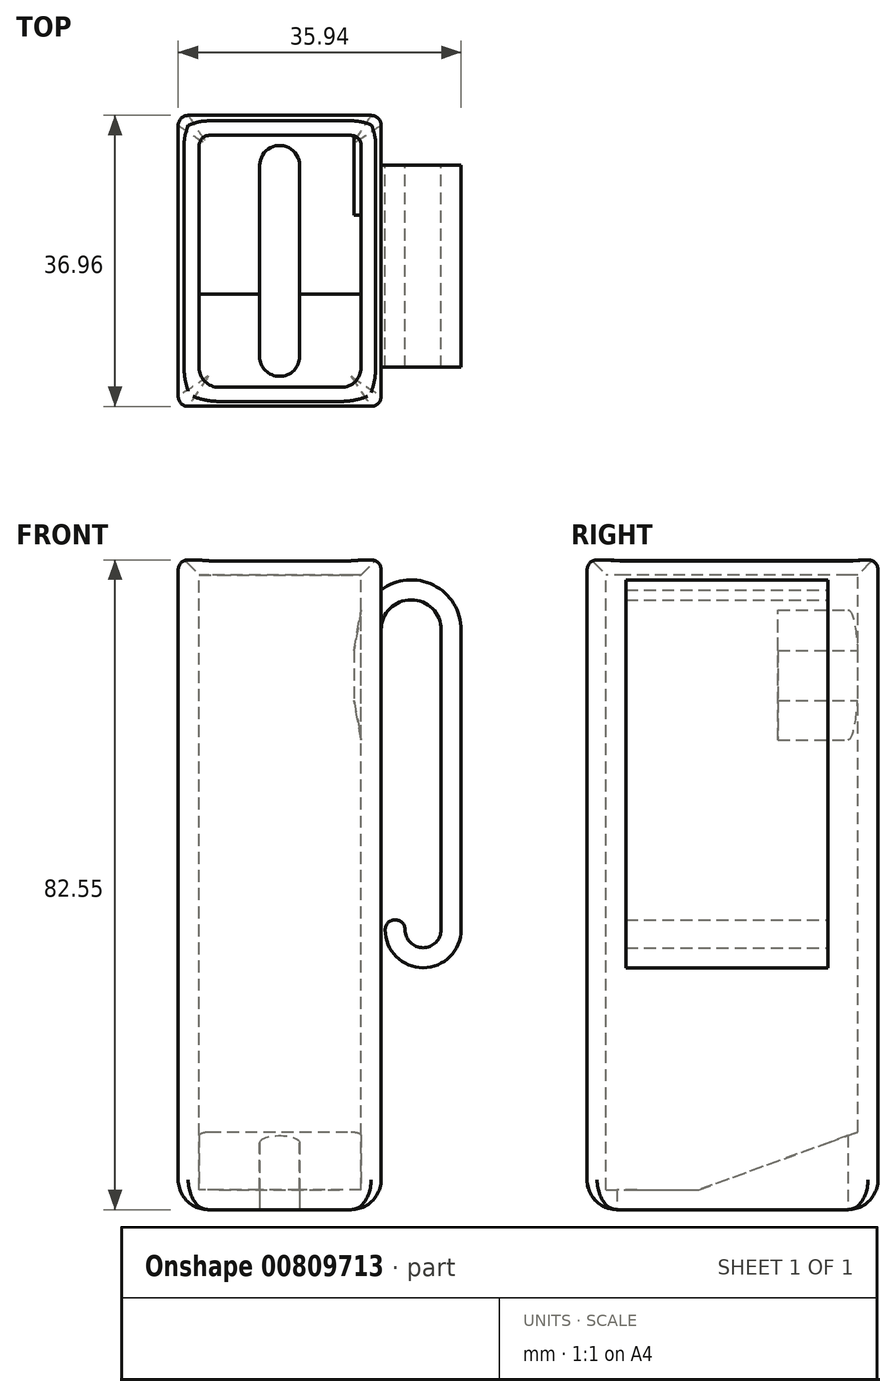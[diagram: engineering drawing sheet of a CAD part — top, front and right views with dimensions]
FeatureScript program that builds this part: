
annotation { "Feature Type Name" : "Feature", "Feature Type Description" : "" }
export const myFeature = defineFeature(function(context is Context, id is Id, definition is map)
    precondition{}
    {
        {
            var Q0;
            Q0=qCreatedBy(makeId("Front.planeOp"),FACE);
            var sketch = newSketch(context, id + "F0", { "sketchPlane" : qUnion([Q0])});
            skLineSegment(sketch, "E0.bottom", {"start": v(-10.35, 0) * mm, "end": v(10.35, 0) * mm});
            skLineSegment(sketch, "E0.top", {"start": v(-10.35, 82.55) * mm, "end": v(10.35, 82.55) * mm});
            skLineSegment(sketch, "E0.left", {"start": v(-10.35, 0) * mm, "end": v(-10.35, 82.55) * mm});
            skLineSegment(sketch, "E0.right", {"start": v(10.35, 0) * mm, "end": v(10.35, 82.55) * mm});
            skSolve(sketch);
        }
        {
            var Q0;
            Q0 = qSketchRegion(id + "F0", true);
            extrude(context, id + "F1", {"entities" : qUnion([Q0]), "depth" : 31.88 * mm, "offsetDistance" : 25.4 * mm});
        }
        {
            var Q0;
            Q0=makeQuery(id+"F1.opExtrude","SWEPT_FACE",FACE,{"disambiguationData":[OSD([sQuery(id+"F0.wireOp",EDGE,"E0.right")])]});
            extrude(context, id + "F2", {"entities" : qUnion([Q0]), "operationType" : NewBodyOperationType.ADD, "depth" : 5.08 * mm, "offsetDistance" : 25.4 * mm});
        }
        {
            var Q0;
            {var subQ0=sQuery(id+"F0.wireOp",EDGE,"E0.right");Q0=makeQuery(id+"F2.boolean.opBoolean","MERGE",FACE,{"derivedFrom":[makeQuery(id+"F1.opExtrude","CAP_FACE",FACE,{"disambiguationData":[OSD([sQuery(id+"F0.wireOp",EDGE,"E0.bottom"),sQuery(id+"F0.wireOp",EDGE,"E0.top"),sQuery(id+"F0.wireOp",EDGE,"E0.left"),subQ0])],"isStart":false}),makeQuery(id+"F2.opExtrude","SWEPT_FACE",FACE,{"disambiguationData":[OSD([subQ0]),TDD([makeQuery(id+"F1.opExtrude","CAP_EDGE",EDGE,{"disambiguationData":[OSD([subQ0])],"isStart":false})])]})]});}
            extrude(context, id + "F3", {"entities" : qUnion([Q0]), "operationType" : NewBodyOperationType.ADD, "depth" : 5.08 * mm, "offsetDistance" : 25.4 * mm});
        }
        {
            var Q0;
            {var subQ0=sQuery(id+"F0.wireOp",EDGE,"E0.right");var subQ1=sQuery(id+"F0.wireOp",EDGE,"E0.bottom");Q0=makeQuery(id+"F2.boolean.opBoolean","MERGE",EDGE,{"derivedFrom":[makeQuery(id+"F1.opExtrude","CAP_EDGE",EDGE,{"disambiguationData":[OSD([subQ1])],"isStart":true}),makeQuery(id+"F2.opExtrude","SWEPT_EDGE",EDGE,{"disambiguationData":[OSD([subQ1,subQ0]),TDD([makeQuery(id+"F1.opExtrude","CAP_VERTEX",VERTEX,{"disambiguationData":[OSD([subQ1,subQ0])],"isStart":true})])]})]});}
            cPlane(context, id + "F4", {"entities" : qUnion([Q0]), "cplaneType" : CPlaneType.LINE_ANGLE, "offset" : 25.4 * mm, "angle" : 70 * degree, "oppositeDirection" : true, "width" : 152.4 * mm, "height" : 152.4 * mm});
        }
        {
            var Q0;
            Q0=qCreatedBy(id+"F4.planeOp",FACE);
            cPlane(context, id + "F5", {"entities" : qUnion([Q0]), "cplaneType" : CPlaneType.OFFSET, "offset" : 10.16 * mm, "oppositeDirection" : true, "width" : 152.4 * mm, "height" : 152.4 * mm});
        }
        {
            var Q0;
            {var subQ0=sQuery(id+"F0.wireOp",EDGE,"E0.right");var subQ1=sQuery(id+"F0.wireOp",EDGE,"E0.top");Q0=makeQuery(id+"F3.boolean.opBoolean","MERGE",FACE,{"derivedFrom":[makeQuery(id+"F2.boolean.opBoolean","MERGE",FACE,{"derivedFrom":[makeQuery(id+"F1.opExtrude","SWEPT_FACE",FACE,{"disambiguationData":[OSD([subQ1])]}),makeQuery(id+"F2.opExtrude","SWEPT_FACE",FACE,{"disambiguationData":[OSD([subQ1,subQ0])]})]}),makeQuery(id+"F3.opExtrude","SWEPT_FACE",FACE,{"disambiguationData":[OSD([subQ1,subQ0])]})]});}
            var sketch = newSketch(context, id + "F6", { "sketchPlane" : qUnion([Q0])});
            skLineSegment(sketch, "E1.bottom", {"start": v(-7.68, -2.54) * mm, "end": v(12.9, -2.54) * mm});
            skLineSegment(sketch, "E1.top", {"start": v(-7.68, -34.54) * mm, "end": v(12.9, -34.54) * mm});
            skLineSegment(sketch, "E1.left", {"start": v(-7.68, -2.54) * mm, "end": v(-7.68, -34.54) * mm});
            skLineSegment(sketch, "E1.right", {"start": v(12.9, -2.54) * mm, "end": v(12.9, -34.54) * mm});
            skSolve(sketch);
        }
        {
            var Q0;
            Q0 = qSketchRegion(id + "F6", true);
            var Q1;
            Q1=qCreatedBy(id+"F5.planeOp",FACE);
            extrude(context, id + "F7", {"entities" : qUnion([Q0]), "operationType" : NewBodyOperationType.REMOVE, "endBound" : BoundingType.UP_TO_SURFACE, "oppositeDirection" : true, "depth" : 25.4 * mm, "endBoundEntityFace" : qUnion([Q1]), "offsetDistance" : 25.4 * mm});
        }
        {
            var Q0;
            Q0=qCreatedBy(makeId("Right.planeOp"),FACE);
            var sketch = newSketch(context, id + "F8", { "sketchPlane" : qUnion([Q0])});
            skLineSegment(sketch, "E2.bottom", {"start": v(-34.93, 0) * mm, "end": v(-22.23, 0) * mm});
            skLineSegment(sketch, "E2.top", {"start": v(-34.93, 2.54) * mm, "end": v(-22.23, 2.54) * mm});
            skLineSegment(sketch, "E2.left", {"start": v(-34.93, 0) * mm, "end": v(-34.93, 2.54) * mm});
            skLineSegment(sketch, "E2.right", {"start": v(-22.23, 0) * mm, "end": v(-22.23, 2.54) * mm});
            skSolve(sketch);
        }
        {
            var Q0;
            Q0 = qSketchRegion(id + "F8", true);
            var Q1;
            Q1=makeQuery(id+"F7.boolean.opBoolean","COPY",FACE,{"derivedFrom":makeQuery(id+"F7.opExtrude","SWEPT_FACE",FACE,{"disambiguationData":[OSD([sQuery(id+"F6.wireOp",EDGE,"E1.left")])]})});
            var Q2;
            Q2=makeQuery(id+"F7.boolean.opBoolean","COPY",FACE,{"derivedFrom":makeQuery(id+"F7.opExtrude","SWEPT_FACE",FACE,{"disambiguationData":[OSD([sQuery(id+"F6.wireOp",EDGE,"E1.right")])]})});
            extrude(context, id + "F9", {"entities" : qUnion([Q0]), "operationType" : NewBodyOperationType.ADD, "endBound" : BoundingType.UP_TO_SURFACE, "oppositeDirection" : true, "depth" : 25.4 * mm, "endBoundEntityFace" : qUnion([Q1]), "offsetDistance" : 25.4 * mm, "hasSecondDirection" : true, "secondDirectionBound" : SecondDirectionBoundingType.UP_TO_SURFACE, "secondDirectionOppositeDirection" : false, "secondDirectionDepth" : 25.4 * mm, "secondDirectionBoundEntityFace" : qUnion([Q2])});
        }
        {
            var Q0;
            {var subQ0=sQuery(id+"F0.wireOp",EDGE,"E0.right");var subQ1=sQuery(id+"F0.wireOp",EDGE,"E0.bottom");Q0=makeQuery(id+"F9.boolean.opBoolean","MERGE",FACE,{"derivedFrom":[makeQuery(id+"F3.boolean.opBoolean","MERGE",FACE,{"derivedFrom":[makeQuery(id+"F2.boolean.opBoolean","MERGE",FACE,{"derivedFrom":[makeQuery(id+"F1.opExtrude","SWEPT_FACE",FACE,{"disambiguationData":[OSD([subQ1])]}),makeQuery(id+"F2.opExtrude","SWEPT_FACE",FACE,{"disambiguationData":[OSD([subQ1,subQ0])]})]}),makeQuery(id+"F3.opExtrude","SWEPT_FACE",FACE,{"disambiguationData":[OSD([subQ1,subQ0])]})]}),makeQuery(id+"F9.opExtrude","SWEPT_FACE",FACE,{"disambiguationData":[OSD([sQuery(id+"F8.wireOp",EDGE,"E2.bottom")])]})]});}
            var sketch = newSketch(context, id + "F10", { "sketchPlane" : qUnion([Q0])});
            skPoint(sketch, "E3.startSnap0", {"position": v(2.54, 36.96) * mm});
            skLineSegment(sketch, "E4.left", {"start": v(0, 30.6) * mm, "end": v(0, 6.35) * mm});
            skLineSegment(sketch, "E4.right", {"start": v(5.08, 30.6) * mm, "end": v(5.08, 6.35) * mm});
            skArc(sketch, "E5", {"start": v(0, 30.6) * mm, "mid": v(2.54, 33.15) * mm, "end": v(5.08, 30.6) * mm});
            skArc(sketch, "E6", {"start": v(0, 6.35) * mm, "mid": v(2.54, 3.8) * mm, "end": v(5.08, 6.35) * mm});
            skSolve(sketch);
        }
        {
            var Q0;
            Q0 = qSketchRegion(id + "F10", true);
            extrude(context, id + "F11", {"entities" : qUnion([Q0]), "operationType" : NewBodyOperationType.REMOVE, "oppositeDirection" : true, "depth" : 25.4 * mm, "offsetDistance" : 25.4 * mm});
        }
        {
            var Q0;
            Q0=makeQuery(id+"F7.boolean.opBoolean","COPY",EDGE,{"derivedFrom":makeQuery(id+"F7.opExtrude","SWEPT_EDGE",EDGE,{"disambiguationData":[OSD([sQuery(id+"F6.wireOp",EDGE,"E1.top"),sQuery(id+"F6.wireOp",EDGE,"E1.right")])]})});
            var Q1;
            Q1=makeQuery(id+"F7.boolean.opBoolean","COPY",EDGE,{"derivedFrom":makeQuery(id+"F7.opExtrude","SWEPT_EDGE",EDGE,{"disambiguationData":[OSD([sQuery(id+"F6.wireOp",EDGE,"E1.top"),sQuery(id+"F6.wireOp",EDGE,"E1.left")])]})});
            fillet(context, id + "F12", {"entities" : qUnion([Q0, Q1]), "radius" : 2.54 * mm, "tangentPropagation" : true, "allowEdgeOverflow" : false});
        }
        {
            var Q0;
            Q0=makeQuery(id+"F7.boolean.opBoolean","COPY",EDGE,{"derivedFrom":makeQuery(id+"F7.opExtrude","SWEPT_EDGE",EDGE,{"disambiguationData":[OSD([sQuery(id+"F6.wireOp",EDGE,"E1.bottom"),sQuery(id+"F6.wireOp",EDGE,"E1.right")])]})});
            var Q1;
            Q1=makeQuery(id+"F7.boolean.opBoolean","COPY",EDGE,{"derivedFrom":makeQuery(id+"F7.opExtrude","SWEPT_EDGE",EDGE,{"disambiguationData":[OSD([sQuery(id+"F6.wireOp",EDGE,"E1.bottom"),sQuery(id+"F6.wireOp",EDGE,"E1.left")])]})});
            fillet(context, id + "F13", {"entities" : qUnion([Q0, Q1]), "radius" : 1.27 * mm, "tangentPropagation" : true, "allowEdgeOverflow" : false});
        }
        {
            var Q0;
            Q0=makeQuery(id+"F7.boolean.opBoolean","COPY",EDGE,{"derivedFrom":makeQuery(id+"F7.opExtrude","CAP_EDGE",EDGE,{"disambiguationData":[OSD([sQuery(id+"F6.wireOp",EDGE,"E1.top")])],"isStart":true})});
            var Q1;
            {var subQ0=sQuery(id+"F0.wireOp",EDGE,"E0.right");var subQ1=sQuery(id+"F0.wireOp",EDGE,"E0.top");Q1=makeQuery(id+"F12.opFillet","BLEND_EDGE",EDGE,{"blendedFrom":[makeQuery(id+"F7.boolean.opBoolean","COPY",EDGE,{"derivedFrom":makeQuery(id+"F7.opExtrude","SWEPT_EDGE",EDGE,{"disambiguationData":[OSD([sQuery(id+"F6.wireOp",EDGE,"E1.top"),sQuery(id+"F6.wireOp",EDGE,"E1.right")])]})}),makeQuery(id+"F3.boolean.opBoolean","MERGE",FACE,{"derivedFrom":[makeQuery(id+"F2.boolean.opBoolean","MERGE",FACE,{"derivedFrom":[makeQuery(id+"F1.opExtrude","SWEPT_FACE",FACE,{"disambiguationData":[OSD([subQ1])]}),makeQuery(id+"F2.opExtrude","SWEPT_FACE",FACE,{"disambiguationData":[OSD([subQ1,subQ0])]})]}),makeQuery(id+"F3.opExtrude","SWEPT_FACE",FACE,{"disambiguationData":[OSD([subQ1,subQ0])]})]})],"blendedInto":[makeQuery(id+"F3.boolean.opBoolean","MERGE",FACE,{"derivedFrom":[makeQuery(id+"F2.boolean.opBoolean","MERGE",FACE,{"derivedFrom":[makeQuery(id+"F1.opExtrude","SWEPT_FACE",FACE,{"disambiguationData":[OSD([subQ1])]}),makeQuery(id+"F2.opExtrude","SWEPT_FACE",FACE,{"disambiguationData":[OSD([subQ1,subQ0])]})]}),makeQuery(id+"F3.opExtrude","SWEPT_FACE",FACE,{"disambiguationData":[OSD([subQ1,subQ0])]})]})]});}
            var Q2;
            Q2=makeQuery(id+"F7.boolean.opBoolean","COPY",EDGE,{"derivedFrom":makeQuery(id+"F7.opExtrude","CAP_EDGE",EDGE,{"disambiguationData":[OSD([sQuery(id+"F6.wireOp",EDGE,"E1.right")])],"isStart":true})});
            var Q3;
            {var subQ0=sQuery(id+"F0.wireOp",EDGE,"E0.right");var subQ1=sQuery(id+"F0.wireOp",EDGE,"E0.top");Q3=makeQuery(id+"F13.opFillet","BLEND_EDGE",EDGE,{"blendedFrom":[makeQuery(id+"F7.boolean.opBoolean","COPY",EDGE,{"derivedFrom":makeQuery(id+"F7.opExtrude","SWEPT_EDGE",EDGE,{"disambiguationData":[OSD([sQuery(id+"F6.wireOp",EDGE,"E1.bottom"),sQuery(id+"F6.wireOp",EDGE,"E1.left")])]})}),makeQuery(id+"F3.boolean.opBoolean","MERGE",FACE,{"derivedFrom":[makeQuery(id+"F2.boolean.opBoolean","MERGE",FACE,{"derivedFrom":[makeQuery(id+"F1.opExtrude","SWEPT_FACE",FACE,{"disambiguationData":[OSD([subQ1])]}),makeQuery(id+"F2.opExtrude","SWEPT_FACE",FACE,{"disambiguationData":[OSD([subQ1,subQ0])]})]}),makeQuery(id+"F3.opExtrude","SWEPT_FACE",FACE,{"disambiguationData":[OSD([subQ1,subQ0])]})]})],"blendedInto":[makeQuery(id+"F3.boolean.opBoolean","MERGE",FACE,{"derivedFrom":[makeQuery(id+"F2.boolean.opBoolean","MERGE",FACE,{"derivedFrom":[makeQuery(id+"F1.opExtrude","SWEPT_FACE",FACE,{"disambiguationData":[OSD([subQ1])]}),makeQuery(id+"F2.opExtrude","SWEPT_FACE",FACE,{"disambiguationData":[OSD([subQ1,subQ0])]})]}),makeQuery(id+"F3.opExtrude","SWEPT_FACE",FACE,{"disambiguationData":[OSD([subQ1,subQ0])]})]})]});}
            var Q4;
            Q4=makeQuery(id+"F7.boolean.opBoolean","COPY",EDGE,{"derivedFrom":makeQuery(id+"F7.opExtrude","CAP_EDGE",EDGE,{"disambiguationData":[OSD([sQuery(id+"F6.wireOp",EDGE,"E1.bottom")])],"isStart":true})});
            var Q5;
            {var subQ0=sQuery(id+"F0.wireOp",EDGE,"E0.right");var subQ1=sQuery(id+"F0.wireOp",EDGE,"E0.top");Q5=makeQuery(id+"F13.opFillet","BLEND_EDGE",EDGE,{"blendedFrom":[makeQuery(id+"F7.boolean.opBoolean","COPY",EDGE,{"derivedFrom":makeQuery(id+"F7.opExtrude","SWEPT_EDGE",EDGE,{"disambiguationData":[OSD([sQuery(id+"F6.wireOp",EDGE,"E1.bottom"),sQuery(id+"F6.wireOp",EDGE,"E1.right")])]})}),makeQuery(id+"F3.boolean.opBoolean","MERGE",FACE,{"derivedFrom":[makeQuery(id+"F2.boolean.opBoolean","MERGE",FACE,{"derivedFrom":[makeQuery(id+"F1.opExtrude","SWEPT_FACE",FACE,{"disambiguationData":[OSD([subQ1])]}),makeQuery(id+"F2.opExtrude","SWEPT_FACE",FACE,{"disambiguationData":[OSD([subQ1,subQ0])]})]}),makeQuery(id+"F3.opExtrude","SWEPT_FACE",FACE,{"disambiguationData":[OSD([subQ1,subQ0])]})]})],"blendedInto":[makeQuery(id+"F3.boolean.opBoolean","MERGE",FACE,{"derivedFrom":[makeQuery(id+"F2.boolean.opBoolean","MERGE",FACE,{"derivedFrom":[makeQuery(id+"F1.opExtrude","SWEPT_FACE",FACE,{"disambiguationData":[OSD([subQ1])]}),makeQuery(id+"F2.opExtrude","SWEPT_FACE",FACE,{"disambiguationData":[OSD([subQ1,subQ0])]})]}),makeQuery(id+"F3.opExtrude","SWEPT_FACE",FACE,{"disambiguationData":[OSD([subQ1,subQ0])]})]})]});}
            var Q6;
            Q6=makeQuery(id+"F7.boolean.opBoolean","COPY",EDGE,{"derivedFrom":makeQuery(id+"F7.opExtrude","CAP_EDGE",EDGE,{"disambiguationData":[OSD([sQuery(id+"F6.wireOp",EDGE,"E1.left")])],"isStart":true})});
            var Q7;
            {var subQ0=sQuery(id+"F0.wireOp",EDGE,"E0.right");var subQ1=sQuery(id+"F0.wireOp",EDGE,"E0.top");Q7=makeQuery(id+"F12.opFillet","BLEND_EDGE",EDGE,{"blendedFrom":[makeQuery(id+"F7.boolean.opBoolean","COPY",EDGE,{"derivedFrom":makeQuery(id+"F7.opExtrude","SWEPT_EDGE",EDGE,{"disambiguationData":[OSD([sQuery(id+"F6.wireOp",EDGE,"E1.top"),sQuery(id+"F6.wireOp",EDGE,"E1.left")])]})}),makeQuery(id+"F3.boolean.opBoolean","MERGE",FACE,{"derivedFrom":[makeQuery(id+"F2.boolean.opBoolean","MERGE",FACE,{"derivedFrom":[makeQuery(id+"F1.opExtrude","SWEPT_FACE",FACE,{"disambiguationData":[OSD([subQ1])]}),makeQuery(id+"F2.opExtrude","SWEPT_FACE",FACE,{"disambiguationData":[OSD([subQ1,subQ0])]})]}),makeQuery(id+"F3.opExtrude","SWEPT_FACE",FACE,{"disambiguationData":[OSD([subQ1,subQ0])]})]})],"blendedInto":[makeQuery(id+"F3.boolean.opBoolean","MERGE",FACE,{"derivedFrom":[makeQuery(id+"F2.boolean.opBoolean","MERGE",FACE,{"derivedFrom":[makeQuery(id+"F1.opExtrude","SWEPT_FACE",FACE,{"disambiguationData":[OSD([subQ1])]}),makeQuery(id+"F2.opExtrude","SWEPT_FACE",FACE,{"disambiguationData":[OSD([subQ1,subQ0])]})]}),makeQuery(id+"F3.opExtrude","SWEPT_FACE",FACE,{"disambiguationData":[OSD([subQ1,subQ0])]})]})]});}
            chamfer(context, id + "F14", {"entities" : qUnion([Q0, Q1, Q2, Q3, Q4, Q5, Q6, Q7]), "width" : 1.9 * mm, "tangentPropagation" : true});
        }
        {
            var Q0;
            {var subQ0=sQuery(id+"F0.wireOp",EDGE,"E0.right");var subQ1=sQuery(id+"F0.wireOp",EDGE,"E0.top");Q0=makeQuery(id+"F3.boolean.opBoolean","MERGE",FACE,{"derivedFrom":[makeQuery(id+"F2.boolean.opBoolean","MERGE",FACE,{"derivedFrom":[makeQuery(id+"F1.opExtrude","SWEPT_FACE",FACE,{"disambiguationData":[OSD([subQ1])]}),makeQuery(id+"F2.opExtrude","SWEPT_FACE",FACE,{"disambiguationData":[OSD([subQ1,subQ0])]})]}),makeQuery(id+"F3.opExtrude","SWEPT_FACE",FACE,{"disambiguationData":[OSD([subQ1,subQ0])]})]});}
            fillet(context, id + "F15", {"entities" : qUnion([Q0]), "radius" : 1.27 * mm, "tangentPropagation" : true, "allowEdgeOverflow" : false});
        }
        {
            var Q0;
            Q0=makeQuery(id+"F3.opExtrude","CAP_EDGE",EDGE,{"disambiguationData":[OSD([sQuery(id+"F0.wireOp",EDGE,"E0.bottom"),sQuery(id+"F0.wireOp",EDGE,"E0.right")])],"isStart":false});
            var Q1;
            {var subQ0=sQuery(id+"F0.wireOp",EDGE,"E0.left");var subQ1=sQuery(id+"F0.wireOp",EDGE,"E0.bottom");Q1=makeQuery(id+"F3.boolean.opBoolean","MERGE",EDGE,{"derivedFrom":[makeQuery(id+"F1.opExtrude","SWEPT_EDGE",EDGE,{"disambiguationData":[OSD([subQ1,subQ0])]}),makeQuery(id+"F3.opExtrude","SWEPT_EDGE",EDGE,{"disambiguationData":[OSD([subQ1,subQ0])]})]});}
            var Q2;
            {var subQ0=sQuery(id+"F0.wireOp",EDGE,"E0.right");var subQ1=sQuery(id+"F0.wireOp",EDGE,"E0.bottom");Q2=makeQuery(id+"F3.boolean.opBoolean","MERGE",EDGE,{"derivedFrom":[makeQuery(id+"F2.opExtrude","CAP_EDGE",EDGE,{"disambiguationData":[OSD([subQ1,subQ0])],"isStart":false}),makeQuery(id+"F3.opExtrude","SWEPT_EDGE",EDGE,{"disambiguationData":[OSD([subQ1,subQ0])]})]});}
            var Q3;
            {var subQ0=sQuery(id+"F0.wireOp",EDGE,"E0.right");var subQ1=sQuery(id+"F0.wireOp",EDGE,"E0.bottom");Q3=makeQuery(id+"F2.boolean.opBoolean","MERGE",EDGE,{"derivedFrom":[makeQuery(id+"F1.opExtrude","CAP_EDGE",EDGE,{"disambiguationData":[OSD([subQ1])],"isStart":true}),makeQuery(id+"F2.opExtrude","SWEPT_EDGE",EDGE,{"disambiguationData":[OSD([subQ1,subQ0]),TDD([makeQuery(id+"F1.opExtrude","CAP_VERTEX",VERTEX,{"disambiguationData":[OSD([subQ1,subQ0])],"isStart":true})])]})]});}
            fillet(context, id + "F16", {"entities" : qUnion([Q0, Q1, Q2, Q3]), "radius" : 3.8 * mm, "tangentPropagation" : true, "allowEdgeOverflow" : false});
        }
        {
            var Q0;
            {var subQ0=sQuery(id+"F0.wireOp",EDGE,"E0.left");var subQ1=sQuery(id+"F0.wireOp",EDGE,"E0.bottom");Q0=makeQuery(id+"F16.opFillet","BLEND_EDGE",EDGE,{"blendedFrom":[makeQuery(id+"F3.opExtrude","CAP_EDGE",EDGE,{"disambiguationData":[OSD([subQ1,sQuery(id+"F0.wireOp",EDGE,"E0.right")])],"isStart":false}),makeQuery(id+"F3.boolean.opBoolean","MERGE",EDGE,{"derivedFrom":[makeQuery(id+"F1.opExtrude","SWEPT_EDGE",EDGE,{"disambiguationData":[OSD([subQ1,subQ0])]}),makeQuery(id+"F3.opExtrude","SWEPT_EDGE",EDGE,{"disambiguationData":[OSD([subQ1,subQ0])]})]})],"blendedInto":[]});}
            var Q1;
            {var subQ0=sQuery(id+"F0.wireOp",EDGE,"E0.right");var subQ1=sQuery(id+"F0.wireOp",EDGE,"E0.bottom");Q1=makeQuery(id+"F16.opFillet","BLEND_EDGE",EDGE,{"blendedFrom":[makeQuery(id+"F3.opExtrude","CAP_EDGE",EDGE,{"disambiguationData":[OSD([subQ1,subQ0])],"isStart":false}),makeQuery(id+"F3.boolean.opBoolean","MERGE",EDGE,{"derivedFrom":[makeQuery(id+"F2.opExtrude","CAP_EDGE",EDGE,{"disambiguationData":[OSD([subQ1,subQ0])],"isStart":false}),makeQuery(id+"F3.opExtrude","SWEPT_EDGE",EDGE,{"disambiguationData":[OSD([subQ1,subQ0])]})]})],"blendedInto":[]});}
            var Q2;
            {var subQ0=sQuery(id+"F0.wireOp",EDGE,"E0.right");var subQ1=sQuery(id+"F0.wireOp",EDGE,"E0.bottom");Q2=makeQuery(id+"F16.opFillet","BLEND_EDGE",EDGE,{"blendedFrom":[makeQuery(id+"F2.boolean.opBoolean","MERGE",EDGE,{"derivedFrom":[makeQuery(id+"F1.opExtrude","CAP_EDGE",EDGE,{"disambiguationData":[OSD([subQ1])],"isStart":true}),makeQuery(id+"F2.opExtrude","SWEPT_EDGE",EDGE,{"disambiguationData":[OSD([subQ1,subQ0]),TDD([makeQuery(id+"F1.opExtrude","CAP_VERTEX",VERTEX,{"disambiguationData":[OSD([subQ1,subQ0])],"isStart":true})])]})]}),makeQuery(id+"F3.boolean.opBoolean","MERGE",EDGE,{"derivedFrom":[makeQuery(id+"F2.opExtrude","CAP_EDGE",EDGE,{"disambiguationData":[OSD([subQ1,subQ0])],"isStart":false}),makeQuery(id+"F3.opExtrude","SWEPT_EDGE",EDGE,{"disambiguationData":[OSD([subQ1,subQ0])]})]})],"blendedInto":[]});}
            var Q3;
            {var subQ0=sQuery(id+"F0.wireOp",EDGE,"E0.left");var subQ1=sQuery(id+"F0.wireOp",EDGE,"E0.bottom");var subQ2=sQuery(id+"F0.wireOp",EDGE,"E0.right");Q3=makeQuery(id+"F16.opFillet","BLEND_EDGE",EDGE,{"blendedFrom":[makeQuery(id+"F2.boolean.opBoolean","MERGE",EDGE,{"derivedFrom":[makeQuery(id+"F1.opExtrude","CAP_EDGE",EDGE,{"disambiguationData":[OSD([subQ1])],"isStart":true}),makeQuery(id+"F2.opExtrude","SWEPT_EDGE",EDGE,{"disambiguationData":[OSD([subQ1,subQ2]),TDD([makeQuery(id+"F1.opExtrude","CAP_VERTEX",VERTEX,{"disambiguationData":[OSD([subQ1,subQ2])],"isStart":true})])]})]}),makeQuery(id+"F3.boolean.opBoolean","MERGE",EDGE,{"derivedFrom":[makeQuery(id+"F1.opExtrude","SWEPT_EDGE",EDGE,{"disambiguationData":[OSD([subQ1,subQ0])]}),makeQuery(id+"F3.opExtrude","SWEPT_EDGE",EDGE,{"disambiguationData":[OSD([subQ1,subQ0])]})]})],"blendedInto":[]});}
            var Q4;
            Q4=makeQuery(id+"F3.opExtrude","CAP_EDGE",EDGE,{"disambiguationData":[OSD([sQuery(id+"F0.wireOp",EDGE,"E0.left")])],"isStart":false});
            var Q5;
            Q5=makeQuery(id+"F3.opExtrude","CAP_EDGE",EDGE,{"disambiguationData":[OSD([sQuery(id+"F0.wireOp",EDGE,"E0.right")])],"isStart":false});
            var Q6;
            {var subQ0=sQuery(id+"F0.wireOp",EDGE,"E0.right");Q6=makeQuery(id+"F2.opExtrude","CAP_EDGE",EDGE,{"disambiguationData":[OSD([subQ0]),TDD([makeQuery(id+"F1.opExtrude","CAP_EDGE",EDGE,{"disambiguationData":[OSD([subQ0])],"isStart":true})])],"isStart":false});}
            var Q7;
            Q7=makeQuery(id+"F1.opExtrude","CAP_EDGE",EDGE,{"disambiguationData":[OSD([sQuery(id+"F0.wireOp",EDGE,"E0.left")])],"isStart":true});
            var Q8;
            {var subQ0=sQuery(id+"F0.wireOp",EDGE,"E0.left");var subQ1=sQuery(id+"F0.wireOp",EDGE,"E0.top");var subQ2=sQuery(id+"F0.wireOp",EDGE,"E0.right");Q8=makeQuery(id+"F15.opFillet","BLEND_EDGE",EDGE,{"blendedFrom":[makeQuery(id+"F2.boolean.opBoolean","MERGE",EDGE,{"derivedFrom":[makeQuery(id+"F1.opExtrude","CAP_EDGE",EDGE,{"disambiguationData":[OSD([subQ1])],"isStart":true}),makeQuery(id+"F2.opExtrude","SWEPT_EDGE",EDGE,{"disambiguationData":[OSD([subQ1,subQ2]),TDD([makeQuery(id+"F1.opExtrude","CAP_VERTEX",VERTEX,{"disambiguationData":[OSD([subQ1,subQ2])],"isStart":true})])]})]}),makeQuery(id+"F3.boolean.opBoolean","MERGE",EDGE,{"derivedFrom":[makeQuery(id+"F1.opExtrude","SWEPT_EDGE",EDGE,{"disambiguationData":[OSD([subQ1,subQ0])]}),makeQuery(id+"F3.opExtrude","SWEPT_EDGE",EDGE,{"disambiguationData":[OSD([subQ1,subQ0])]})]})],"blendedInto":[]});}
            fillet(context, id + "F17", {"entities" : qUnion([Q0, Q1, Q2, Q3, Q4, Q5, Q6, Q7, Q8]), "radius" : 1.27 * mm, "tangentPropagation" : true, "allowEdgeOverflow" : false});
        }
        {
            var Q0;
            Q0=qCreatedBy(makeId("Front.planeOp"),FACE);
            var sketch = newSketch(context, id + "F18", { "sketchPlane" : qUnion([Q0])});
            skLineSegment(sketch, "E7.left", {"start": v(12.9, 71.12) * mm, "end": v(12.9, 64.77) * mm});
            skLineSegment(sketch, "E7.right", {"start": v(12, 71.04) * mm, "end": v(12, 64.69) * mm});
            skLineSegment(sketch, "E8", {"start": v(12, 71.04) * mm, "end": v(12.9, 76.2) * mm});
            skLineSegment(sketch, "E9", {"start": v(12.9, 76.2) * mm, "end": v(12.9, 71.12) * mm});
            skLineSegment(sketch, "E10", {"start": v(12, 64.69) * mm, "end": v(12.9, 59.69) * mm});
            skLineSegment(sketch, "E11", {"start": v(12.9, 59.69) * mm, "end": v(12.9, 64.77) * mm});
            skSolve(sketch);
        }
        {
            var Q0;
            Q0 = qSketchRegion(id + "F18", true);
            extrude(context, id + "F19", {"entities" : qUnion([Q0]), "operationType" : NewBodyOperationType.ADD, "depth" : 12.7 * mm, "offsetDistance" : 25.4 * mm});
        }
        {
            var Q0;
            Q0=qCreatedBy(makeId("Front.planeOp"),FACE);
            var sketch = newSketch(context, id + "F20", { "sketchPlane" : qUnion([Q0])});
            skLineSegment(sketch, "E12", {"start": v(12.9, 73.66) * mm, "end": v(12.9, 29.88) * mm});
            skLineSegment(sketch, "E13", {"start": v(12.9, 73.66) * mm, "end": v(17.97, 73.66) * mm});
            skArc(sketch, "E14", {"start": v(12.9, 73.66) * mm, "mid": v(19.24, 80.01) * mm, "end": v(25.6, 73.66) * mm});
            skArc(sketch, "E15", {"start": v(23.05, 73.66) * mm, "mid": v(19.24, 77.47) * mm, "end": v(15.43, 73.66) * mm});
            skLineSegment(sketch, "E16", {"start": v(25.6, 73.66) * mm, "end": v(25.6, 35.56) * mm});
            skLineSegment(sketch, "E17", {"start": v(23.05, 35.56) * mm, "end": v(23.05, 73.66) * mm});
            skArc(sketch, "E18", {"start": v(23.05, 35.56) * mm, "mid": v(20.76, 33.27) * mm, "end": v(18.48, 35.56) * mm});
            skArc(sketch, "E19", {"start": v(25.6, 35.56) * mm, "mid": v(20.76, 30.73) * mm, "end": v(15.94, 35.56) * mm});
            skArc(sketch, "E20", {"start": v(18.48, 35.56) * mm, "mid": v(17.2, 36.83) * mm, "end": v(15.94, 35.56) * mm});
            skSolve(sketch);
        }
        {
            var Q0;
            Q0 = qSketchRegion(id + "F20", true);
            extrude(context, id + "F21", {"entities" : qUnion([Q0]), "operationType" : NewBodyOperationType.ADD, "depth" : 32 * mm, "offsetDistance" : 25.4 * mm, "hasSecondDirection" : true, "secondDirectionOppositeDirection" : false, "secondDirectionDepth" : 6.35 * mm});
        }
    });
